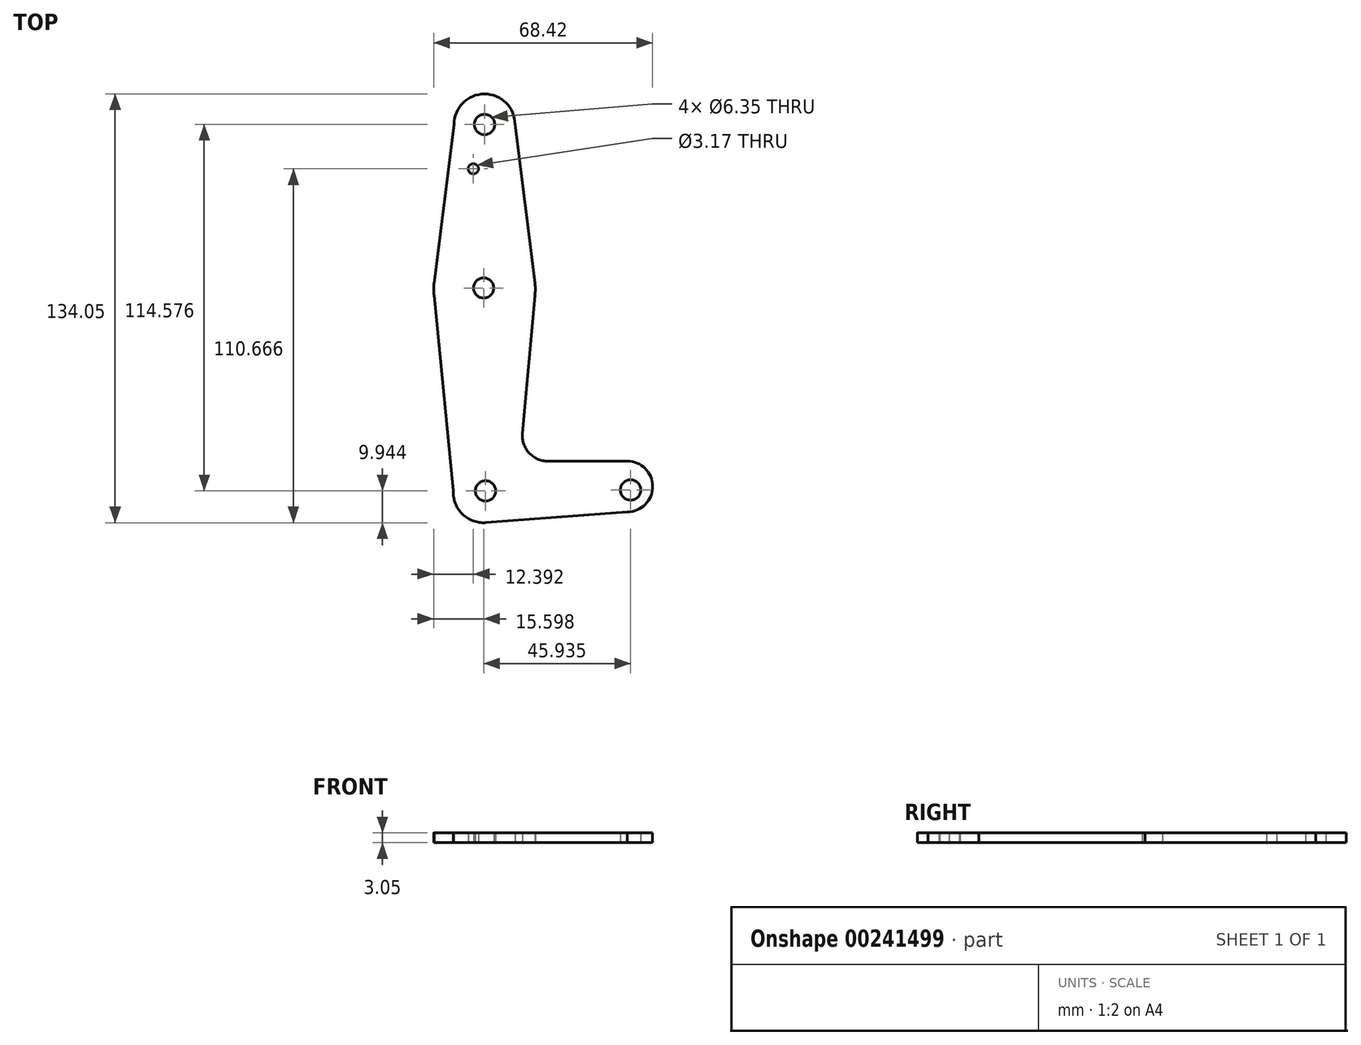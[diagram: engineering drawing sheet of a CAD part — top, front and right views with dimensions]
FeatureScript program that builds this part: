
annotation { "Feature Type Name" : "Feature", "Feature Type Description" : "" }
export const myFeature = defineFeature(function(context is Context, id is Id, definition is map)
    precondition{}
    {
        {
            var Q0;
            Q0=qCreatedBy(makeId("Top.planeOp"),FACE);
            var sketch = newSketch(context, id + "F0", { "sketchPlane" : qUnion([Q0])});
            skCircle(sketch, "E0", {"center": v(0, 114.3) * mm, "radius": 9.53 * mm});
            skCircle(sketch, "E1", {"center": v(-0.26, -0.7) * mm, "radius": 9.53 * mm});
            skCircle(sketch, "E2", {"center": v(44.6, 1.1) * mm, "radius": 7.94 * mm});
            skCircle(sketch, "E3", {"center": v(0, 62.85) * mm, "radius": 15.88 * mm});
            skLineSegment(sketch, "E4", {"start": v(9.52, 114.3) * mm, "end": v(15.75, 64.84) * mm});
            skLineSegment(sketch, "E5", {"start": v(-9.53, 114.3) * mm, "end": v(-15.75, 64.84) * mm});
            skLineSegment(sketch, "E6", {"start": v(-9.78, -0.26) * mm, "end": v(-15.75, 60.87) * mm});
            skLineSegment(sketch, "E7", {"start": v(44.6, 9.03) * mm, "end": v(19.79, 9.03) * mm});
            skLineSegment(sketch, "E8", {"start": v(44.6, -6.84) * mm, "end": v(0, -10.23) * mm});
            skLineSegment(sketch, "E9", {"start": v(11.87, 17.7) * mm, "end": v(15.75, 60.87) * mm});
            skCircle(sketch, "E10", {"center": v(0, 114.3) * mm, "radius": 3.18 * mm});
            skCircle(sketch, "E11", {"center": v(-0.28, 63.19) * mm, "radius": 3.18 * mm});
            skCircle(sketch, "E12", {"center": v(0.32, -0.28) * mm, "radius": 3.18 * mm});
            skCircle(sketch, "E13", {"center": v(45.65, 0.03) * mm, "radius": 3.18 * mm});
            skCircle(sketch, "E14", {"center": v(-3.49, 100.45) * mm, "radius": 1.59 * mm});
            skArc(sketch, "E15.filletArc", {"start": v(11.87, 17.7) * mm, "mid": v(13.92, 11.62) * mm, "end": v(19.79, 9.03) * mm});
            skSolve(sketch);
        }
        {
            var Q0;
            Q0 = qSketchRegion(id + "F0", true);
            extrude(context, id + "F1", {"entities" : qUnion([Q0]), "depth" : 3.05 * mm});
        }
    });
